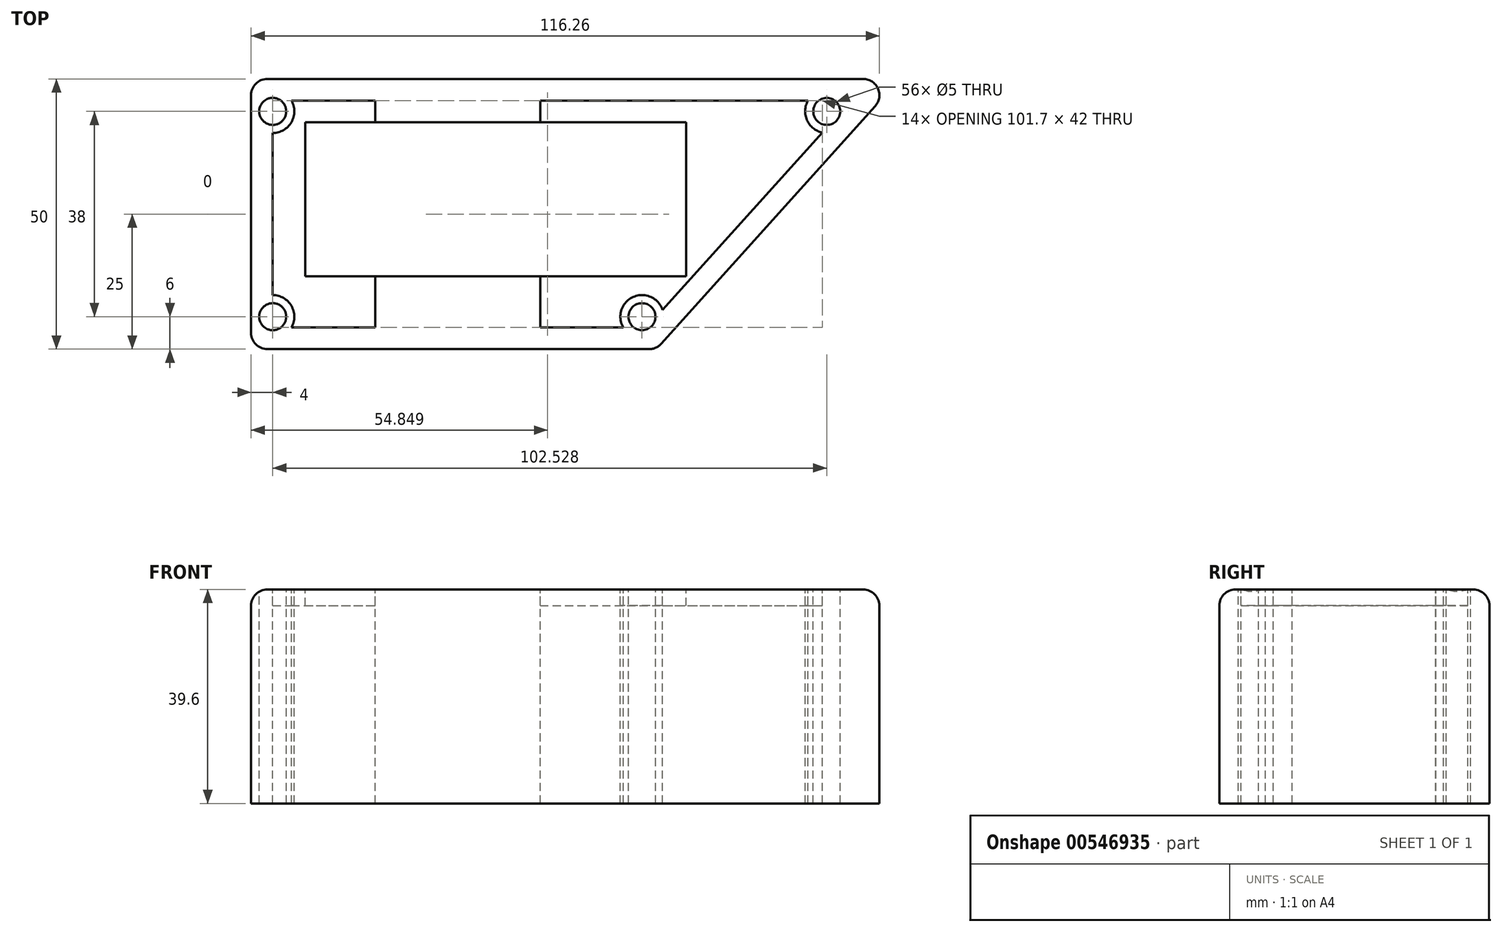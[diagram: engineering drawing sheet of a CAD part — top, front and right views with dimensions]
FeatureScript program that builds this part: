
annotation { "Feature Type Name" : "Feature", "Feature Type Description" : "" }
export const myFeature = defineFeature(function(context is Context, id is Id, definition is map)
    precondition{}
    {
        {
            var Q0;
            Q0=qCreatedBy(makeId("Top.planeOp"),FACE);
            var sketch = newSketch(context, id + "F0", { "sketchPlane" : qUnion([Q0])});
            skLineSegment(sketch, "E0", {"start": v(0, 0) * mm, "end": v(120, 0) * mm});
            skLineSegment(sketch, "E1", {"start": v(0, 0) * mm, "end": v(0, -50) * mm});
            skLineSegment(sketch, "E2", {"start": v(0, -50) * mm, "end": v(75, -50) * mm});
            skLineSegment(sketch, "E3", {"start": v(75, -50) * mm, "end": v(120, 0) * mm});
            skLineSegment(sketch, "E4.0", {"start": v(10, -8) * mm, "end": v(80.5, -8) * mm});
            skLineSegment(sketch, "E5.0", {"start": v(10, -36.5) * mm, "end": v(80.5, -36.5) * mm});
            skLineSegment(sketch, "E6.0", {"start": v(10, -8) * mm, "end": v(10, -36.5) * mm});
            skLineSegment(sketch, "E7.0", {"start": v(80.5, -8) * mm, "end": v(80.5, -36.5) * mm});
            skLineSegment(sketch, "E8.0", {"start": v(23, -3) * mm, "end": v(23, -8) * mm});
            skLineSegment(sketch, "E9.0", {"start": v(53.5, -3) * mm, "end": v(53.5, -8) * mm});
            skLineSegment(sketch, "E10.trimOffspring", {"start": v(23, -36.5) * mm, "end": v(23, -47) * mm});
            skLineSegment(sketch, "E11.trimOffspring", {"start": v(53.5, -36.5) * mm, "end": v(53.5, -47) * mm});
            skLineSegment(sketch, "E12.0", {"start": v(3, -6) * mm, "end": v(6, -6) * mm, "construction": true});
            skLineSegment(sketch, "E13.0", {"start": v(3, -44) * mm, "end": v(6, -44) * mm, "construction": true});
            skLineSegment(sketch, "E14.0", {"start": v(6, -3) * mm, "end": v(6, -6) * mm, "construction": true});
            skLineSegment(sketch, "E15.0", {"start": v(71.43, -45) * mm, "end": v(72.33, -44) * mm, "construction": true});
            skLineSegment(sketch, "E16.trimOffspring", {"start": v(106.53, -6) * mm, "end": v(110.56, -6) * mm, "construction": true});
            skLineSegment(sketch, "E17.trimOffspring", {"start": v(106.53, -6) * mm, "end": v(109.23, -3) * mm, "construction": true});
            skLineSegment(sketch, "E18.trimOffspring", {"start": v(72.33, -44) * mm, "end": v(73.66, -44) * mm, "construction": true});
            skLineSegment(sketch, "E19.trimOffspring", {"start": v(6, -44) * mm, "end": v(6, -47) * mm, "construction": true});
            skCircle(sketch, "E20", {"center": v(72.33, -44) * mm, "radius": 2.5 * mm});
            skCircle(sketch, "E21", {"center": v(106.53, -6) * mm, "radius": 2.5 * mm});
            skArc(sketch, "E22", {"start": v(76.13, -42.76) * mm, "mid": v(70.7, -40.35) * mm, "end": v(68.86, -46) * mm});
            skArc(sketch, "E23", {"start": v(110.53, -6.04) * mm, "mid": v(110.53, -6.02) * mm, "end": v(110.53, -6) * mm});
            skArc(sketch, "E24.trimOffspring", {"start": v(109.2, -3.03) * mm, "mid": v(109.19, -3.01) * mm, "end": v(109.17, -3) * mm});
            skArc(sketch, "E25.trimOffspring", {"start": v(103.06, -4) * mm, "mid": v(102.87, -7.63) * mm, "end": v(105.7, -9.91) * mm});
            skLineSegment(sketch, "E26.trimOffspring", {"start": v(109.17, -3) * mm, "end": v(109.23, -3) * mm});
            skLineSegment(sketch, "E27.trimOffspring", {"start": v(110.53, -6.04) * mm, "end": v(110.56, -6) * mm});
            skLineSegment(sketch, "E28.0", {"start": v(76.13, -42.76) * mm, "end": v(105.7, -9.91) * mm});
            skLineSegment(sketch, "E29.0", {"start": v(7.46, -46) * mm, "end": v(68.86, -46) * mm});
            skLineSegment(sketch, "E30.0", {"start": v(4, -10) * mm, "end": v(4, -40) * mm});
            skLineSegment(sketch, "E31.0", {"start": v(7.46, -4) * mm, "end": v(103.06, -4) * mm});
            skLineSegment(sketch, "E32.0", {"start": v(4, -44) * mm, "end": v(4, -47) * mm});
            skLineSegment(sketch, "E33.0", {"start": v(4, -3) * mm, "end": v(4, -6) * mm});
            skCircle(sketch, "E34", {"center": v(4, -6) * mm, "radius": 2.5 * mm});
            skCircle(sketch, "E35", {"center": v(4, -44) * mm, "radius": 2.5 * mm});
            skArc(sketch, "E36", {"start": v(4, -10) * mm, "mid": v(7.46, -8) * mm, "end": v(7.46, -4) * mm});
            skArc(sketch, "E37", {"start": v(7.46, -46) * mm, "mid": v(7.46, -42) * mm, "end": v(4, -40) * mm});
            skSolve(sketch);
        }
        {
            var Q0;
            {var subQ0=sQuery(id+"F0.wireOp",EDGE,"E6.0");Q0=makeQuery(id+"F0.imprint","IMPRINT",FACE,{"disambiguationData":[TD([[makeQuery(id+"F0.imprint","IMPRINT",EDGE,{"derivedFrom":subQ0}),-1.0]])]});}
            var Q1;
            {var subQ5=sQuery(id+"F0.wireOp",EDGE,"E7.0");Q1=makeQuery(id+"F0.imprint","IMPRINT",FACE,{"disambiguationData":[TD([[makeQuery(id+"F0.imprint","IMPRINT",EDGE,{"derivedFrom":subQ5}),1.0]])]});}
            extrude(context, id + "F1", {"entities" : qUnion([Q0, Q1]), "oppositeDirection" : true, "depth" : 3 * mm, "offsetDistance" : 25 * mm});
        }
        {
            var Q0;
            {var subQ0=sQuery(id+"F0.wireOp",EDGE,"E10.trimOffspring");var subQ1=sQuery(id+"F0.wireOp",EDGE,"E5.0");var subQ2=makeQuery(id+"F0.imprint","INTERSECT",VERTEX,{"derivedFrom":[subQ1,subQ0]});Q0=makeQuery(id+"F0.imprint","IMPRINT",FACE,{"disambiguationData":[TD([[makeQuery(id+"F0.imprint","IMPRINT",EDGE,{"disambiguationData":[TD([[subQ2,-1.0]])],"derivedFrom":subQ1}),-1.0]])]});}
            var Q1;
            {var subQ0=sQuery(id+"F0.wireOp",EDGE,"E8.0");var subQ1=sQuery(id+"F0.wireOp",EDGE,"E4.0");var subQ2=makeQuery(id+"F0.imprint","INTERSECT",VERTEX,{"derivedFrom":[subQ1,subQ0]});Q1=makeQuery(id+"F0.imprint","IMPRINT",FACE,{"disambiguationData":[TD([[makeQuery(id+"F0.imprint","IMPRINT",EDGE,{"disambiguationData":[TD([[subQ2,-1.0]])],"derivedFrom":subQ1}),1.0]])]});}
            var Q2;
            Q2=makeQuery(id+"F0.imprint","IMPRINT",FACE,{"disambiguationData":[TD([[makeQuery(id+"F0.imprint","IMPRINT",EDGE,{"derivedFrom":sQuery(id+"F0.wireOp",EDGE,"E0")}),-1.0]])]});
            extrude(context, id + "F2", {"entities" : qUnion([Q0, Q1, Q2]), "oppositeDirection" : true, "depth" : 39.6 * mm, "offsetDistance" : 25 * mm});
        }
        {
            var Q0;
            Q0=makeQuery(id+"F2.opExtrude","CAP_EDGE",EDGE,{"disambiguationData":[OSD([sQuery(id+"F0.wireOp",EDGE,"E2")])],"isStart":true});
            var Q1;
            Q1=makeQuery(id+"F2.opExtrude","SWEPT_EDGE",EDGE,{"disambiguationData":[OSD([sQuery(id+"F0.wireOp",EDGE,"E1"),sQuery(id+"F0.wireOp",EDGE,"E2")])]});
            var Q2;
            Q2=makeQuery(id+"F2.opExtrude","SWEPT_EDGE",EDGE,{"disambiguationData":[OSD([sQuery(id+"F0.wireOp",EDGE,"E2"),sQuery(id+"F0.wireOp",EDGE,"E3")])]});
            var Q3;
            Q3=makeQuery(id+"F2.opExtrude","CAP_EDGE",EDGE,{"disambiguationData":[OSD([sQuery(id+"F0.wireOp",EDGE,"E3")])],"isStart":true});
            var Q4;
            Q4=makeQuery(id+"F2.opExtrude","SWEPT_EDGE",EDGE,{"disambiguationData":[OSD([sQuery(id+"F0.wireOp",EDGE,"E0"),sQuery(id+"F0.wireOp",EDGE,"E3")])]});
            var Q5;
            Q5=makeQuery(id+"F2.opExtrude","CAP_EDGE",EDGE,{"disambiguationData":[OSD([sQuery(id+"F0.wireOp",EDGE,"E0")])],"isStart":true});
            var Q6;
            Q6=makeQuery(id+"F2.opExtrude","SWEPT_EDGE",EDGE,{"disambiguationData":[OSD([sQuery(id+"F0.wireOp",EDGE,"E0"),sQuery(id+"F0.wireOp",EDGE,"E1")])]});
            var Q7;
            Q7=makeQuery(id+"F2.opExtrude","CAP_EDGE",EDGE,{"disambiguationData":[OSD([sQuery(id+"F0.wireOp",EDGE,"E1")])],"isStart":true});
            fillet(context, id + "F3", {"entities" : qUnion([Q0, Q1, Q2, Q3, Q4, Q5, Q6, Q7]), "radius" : 3 * mm, "tangentPropagation" : true, "allowEdgeOverflow" : false});
        }
    });
